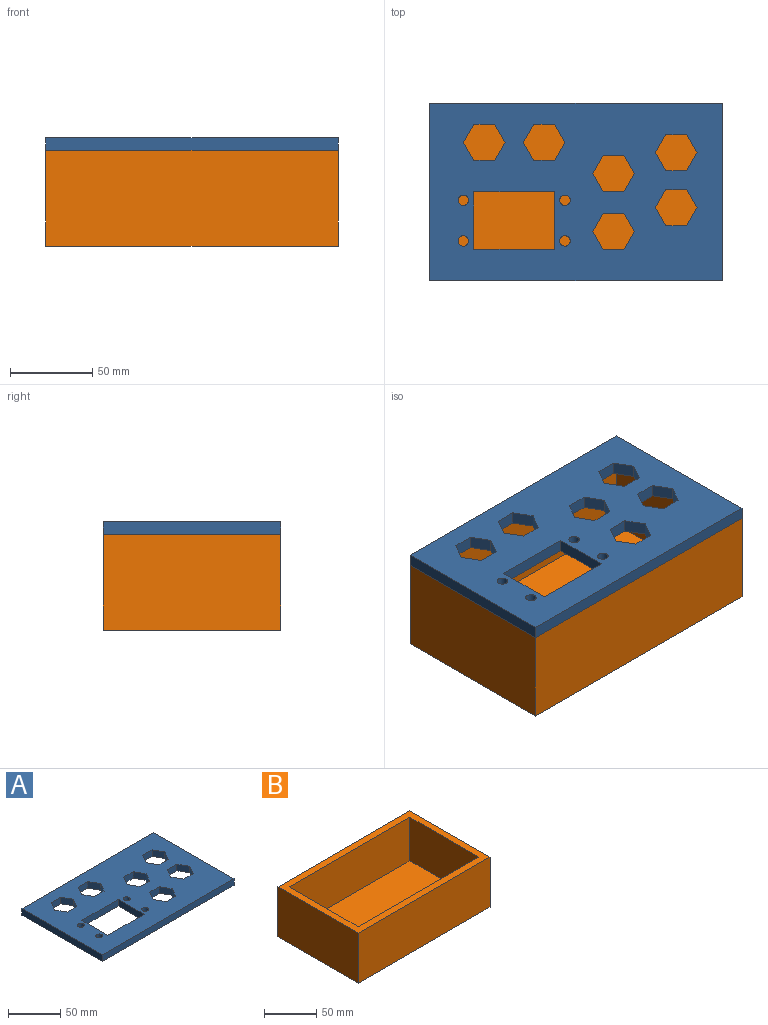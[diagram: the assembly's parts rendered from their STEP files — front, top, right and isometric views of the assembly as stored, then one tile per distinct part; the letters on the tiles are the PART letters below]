
ASSEMBLY  parts=2 mates=1
PART A: 50 faces, bbox 177.8x108x7.6 mm
  f0: plane 177.8x107.95mm, normal (0,0,1), area 14835.7mm2, adj f2,f3,f4,f5,f6,f7,f8,f9
  f1: plane 177.8x107.95mm, normal (0,0,-1), area 14835.7mm2, adj f2,f3,f4,f5,f6,f7,f8,f9
  f2: plane 107.95x7.62mm, normal (1,0,0), area 822.6mm2, adj f0,f1,f3,f5
  f3: plane 177.8x7.62mm, normal (0,1,0), area 1354.8mm2, adj f0,f1,f2,f4
  f4: plane 107.95x7.62mm, normal (-1,0,0), area 822.6mm2, adj f0,f1,f3,f5
  f5: plane 177.8x7.62mm, normal (0,-1,0), area 1354.8mm2, adj f0,f1,f2,f4
  f6: plane 12.7x7.62mm, normal (0,1,0), area 96.8mm2, adj f0,f1,f7,f11
  f7: plane 11x7.62mm, normal (-0.87,0.5,0), area 96.8mm2, adj f0,f1,f6,f8
  f8: plane 11x7.62mm, normal (-0.87,-0.5,0), area 96.8mm2, adj f0,f1,f7,f9
  f9: plane 12.7x7.62mm, normal (0,-1,0), area 96.8mm2, adj f0,f1,f8,f10
  f10: plane 11x7.62mm, normal (0.87,-0.5,0), area 96.8mm2, adj f0,f1,f9,f11
  f11: plane 11x7.62mm, normal (0.87,0.5,0), area 96.8mm2, adj f0,f1,f6,f10
  f12: cylinder r=3.17mm len=7.62mm, axis (0,0,1), area 152mm2, adj f0,f1
  f13: cylinder r=3.17mm len=7.62mm, axis (0,0,1), area 152mm2, adj f0,f1
  f14: plane 12.7x7.62mm, normal (0,1,0), area 96.8mm2, adj f0,f1,f15,f19
  f15: plane 11x7.62mm, normal (-0.87,0.5,0), area 96.8mm2, adj f0,f1,f14,f16
  f16: plane 11x7.62mm, normal (-0.87,-0.5,0), area 96.8mm2, adj f0,f1,f15,f17
  f17: plane 12.7x7.62mm, normal (0,-1,0), area 96.8mm2, adj f0,f1,f16,f18
  f18: plane 11x7.62mm, normal (0.87,-0.5,0), area 96.8mm2, adj f0,f1,f17,f19
  f19: plane 11x7.62mm, normal (0.87,0.5,0), area 96.8mm2, adj f0,f1,f14,f18
  f20: plane 12.7x7.62mm, normal (0,1,0), area 96.8mm2, adj f0,f1,f21,f25
  f21: plane 11x7.62mm, normal (-0.87,0.5,0), area 96.8mm2, adj f0,f1,f20,f22
  f22: plane 11x7.62mm, normal (-0.87,-0.5,0), area 96.8mm2, adj f0,f1,f21,f23
  f23: plane 12.7x7.62mm, normal (0,-1,0), area 96.8mm2, adj f0,f1,f22,f24
  f24: plane 11x7.62mm, normal (0.87,-0.5,0), area 96.8mm2, adj f0,f1,f23,f25
  f25: plane 11x7.62mm, normal (0.87,0.5,0), area 96.8mm2, adj f0,f1,f20,f24
  f26: plane 12.7x7.62mm, normal (0,1,0), area 96.8mm2, adj f0,f1,f27,f31
  f27: plane 11x7.62mm, normal (-0.87,0.5,0), area 96.8mm2, adj f0,f1,f26,f28
  f28: plane 11x7.62mm, normal (-0.87,-0.5,0), area 96.8mm2, adj f0,f1,f27,f29
  f29: plane 12.7x7.62mm, normal (0,-1,0), area 96.8mm2, adj f0,f1,f28,f30
  f30: plane 11x7.62mm, normal (0.87,-0.5,0), area 96.8mm2, adj f0,f1,f29,f31
  f31: plane 11x7.62mm, normal (0.87,0.5,0), area 96.8mm2, adj f0,f1,f26,f30
  f32: plane 12.7x7.62mm, normal (0,1,0), area 96.8mm2, adj f0,f1,f33,f37
  f33: plane 11x7.62mm, normal (-0.87,0.5,0), area 96.8mm2, adj f0,f1,f32,f34
  f34: plane 11x7.62mm, normal (-0.87,-0.5,0), area 96.8mm2, adj f0,f1,f33,f35
  f35: plane 12.7x7.62mm, normal (0,-1,0), area 96.8mm2, adj f0,f1,f34,f36
  f36: plane 11x7.62mm, normal (0.87,-0.5,0), area 96.8mm2, adj f0,f1,f35,f37
  f37: plane 11x7.62mm, normal (0.87,0.5,0), area 96.8mm2, adj f0,f1,f32,f36
  f38: plane 12.7x7.62mm, normal (0,1,0), area 96.8mm2, adj f0,f1,f39,f43
  f39: plane 11x7.62mm, normal (-0.87,0.5,0), area 96.8mm2, adj f0,f1,f38,f40
  f40: plane 11x7.62mm, normal (-0.87,-0.5,0), area 96.8mm2, adj f0,f1,f39,f41
  f41: plane 12.7x7.62mm, normal (0,-1,0), area 96.8mm2, adj f0,f1,f40,f42
  f42: plane 11x7.62mm, normal (0.87,-0.5,0), area 96.8mm2, adj f0,f1,f41,f43
  f43: plane 11x7.62mm, normal (0.87,0.5,0), area 96.8mm2, adj f0,f1,f38,f42
  f44: plane 49.16x7.62mm, normal (0,-1,0), area 374.6mm2, adj f0,f1,f45,f47
  f45: plane 34.93x7.62mm, normal (1,0,0), area 266.1mm2, adj f0,f1,f44,f46
  f46: plane 49.16x7.62mm, normal (0,1,0), area 374.6mm2, adj f0,f1,f45,f47
  f47: plane 34.93x7.62mm, normal (-1,0,0), area 266.1mm2, adj f0,f1,f44,f46
  f48: cylinder r=3.17mm len=7.62mm, axis (0,0,1), area 152mm2, adj f0,f1
  f49: cylinder r=3.17mm len=7.62mm, axis (0,0,1), area 152mm2, adj f0,f1
PART B: 11 faces, bbox 177.8x108x58.4 mm
  f0: plane 162.56x50.8mm, normal (0,1,0), area 8258mm2, adj f1,f7,f8,f9
  f1: plane 92.71x50.8mm, normal (-1,0,0), area 4709.7mm2, adj f0,f2,f8,f9
  f2: plane 162.56x50.8mm, normal (0,-1,0), area 8258mm2, adj f1,f7,f8,f9
  f3: plane 177.8x58.42mm, normal (0,1,0), area 10387.1mm2, adj f4,f6,f8,f10
  f4: plane 107.95x58.42mm, normal (1,0,0), area 6306.4mm2, adj f3,f5,f8,f10
  f5: plane 177.8x58.42mm, normal (0,-1,0), area 10387.1mm2, adj f4,f6,f8,f10
  f6: plane 107.95x58.42mm, normal (-1,0,0), area 6306.4mm2, adj f3,f5,f8,f10
  f7: plane 92.71x50.8mm, normal (1,0,0), area 4709.7mm2, adj f0,f2,f8,f9
  f8: plane 177.8x107.95mm, normal (0,0,1), area 4122.6mm2, adj f0,f1,f2,f3,f4,f5,f6,f7
  f9: plane 162.56x92.71mm, normal (0,0,1), area 15070.9mm2, adj f0,f1,f2,f7
  f10: plane 177.8x107.95mm, normal (0,0,-1), area 19193.5mm2, adj f3,f4,f5,f6
PLACE A rot(axis=(1,0,0),0deg) t=(0,0,0)mm
PLACE B at identity fixed
MATE revolute B.f4 <-> A.f2  axis (1,0,0) through (88.9,-53.98,0)mm
